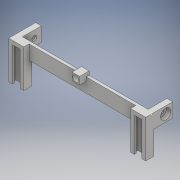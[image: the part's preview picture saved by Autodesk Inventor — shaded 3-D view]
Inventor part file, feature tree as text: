
AUTODESK INVENTOR PART (.ipt)
format: ipt  version: 2018 (Build 220112000, 112)  size: 307,200 bytes
history: native  units: mm
features: sketch x15, extrude x14
ambient origin geometry x8: Origin, YZ Plane, XZ Plane, XY Plane, X Axis, Y Axis, Z Axis, Center Point
bodies: Solid1 (feature_tree)
feature tree (29):
  extrude  "Extrusion1"  Depth=15.0mm
  extrude  "Extrusion2"  Depth=6.0mm
  extrude  "Extrusion3"  Depth=20.0mm TaperAngle=0.0deg
  extrude  "Extrusion4"  Depth=10.0mm
  extrude  "Extrusion5"  Depth=5.0mm
  extrude  "Extrusion6"  Depth=1.5mm TaperAngle=0.0deg
  extrude  "Extrusion7"  Depth=4.0mm
  sketch  "Sketch8"  dims[d19=4.0mm d20=3.0mm d21=0.0mm]
  extrude  "Extrusion8"  Depth=3.0mm TaperAngle=0.0deg
  extrude  "Extrusion9"  Depth=8.0mm
  extrude  "Extrusion10"  Depth=7.5mm TaperAngle=0.0deg
  extrude  "Extrusion11"  Depth=25.0mm
  extrude  "Extrusion12"  Depth=25.0mm
  extrude  "Extrusion13"  Depth=23.0mm
  extrude  "Extrusion14"  Depth=2.0mm
  sketch  "Sketch1"  dims[d0=145.0mm d1=15.0mm]
  sketch  "Sketch2"  dims[d2=3.0mm d3=0.0mm d4=6.0mm]
  sketch  "Sketch3"  dims[d5=6.0mm d6=20.0mm d7=0.0mm]
  sketch  "Sketch4"  dims[d8=12.5mm d9=10.0mm]
  sketch  "Sketch5"  dims[d10=156.0mm d11=0.0mm d12=5.0mm]
  sketch  "Sketch6"  dims[d13=1.5mm d14=0.0mm d15=1.5mm d16=0.0mm]
  sketch  "Sketch7"  dims[d17=4.0mm d18=4.0mm]
  sketch  "Sketch9"  dims[d22=6.4mm d23=8.0mm]
  sketch  "Sketch10"  dims[d24=10.0mm d25=0.0mm d26=7.5mm d27=0.0mm]
  sketch  "Sketch11"  dims[d28=16.0mm d29=25.0mm]
  sketch  "Sketch12"  dims[d30=16.0mm d31=25.0mm]
  sketch  "Sketch13"  dims[d32=2.0mm d33=23.0mm]
  sketch  "Sketch14"  dims[d34=12.0mm d35=2.0mm]
  sketch  "Sketch15"  dims[d36=23.0mm d37=12.0mm d38=3.5mm d39=0.0mm d40=3.0mm d41=0.0mm d42=4.0mm d43=4.0mm d44=4.0mm d45=4.0mm d46=4.0mm d47=2.0mm d48=0.0mm d49=15.0mm d50=16.5mm d51=0.0mm d52=0.0mm d53=11.0mm d54=4.5mm d55=0.0mm d56=4.5mm d57=0.0mm]
